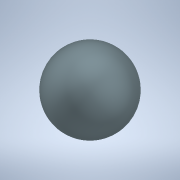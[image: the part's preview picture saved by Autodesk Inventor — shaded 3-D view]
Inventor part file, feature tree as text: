
AUTODESK INVENTOR PART (.ipt)
format: ipt  version: 2022 (Build 260153000, 153)  size: 121,856 bytes
history: native  units: in
note: dims shown in document units (in); Inventor stores cm internally (conversion verified against a paired STEP export)
features: revolve x1, sketch x1
ambient origin geometry x8: Origin, YZ Plane, XZ Plane, XY Plane, X Axis, Y Axis, Z Axis, Center Point
bodies: Solid1 (feature_tree)
feature tree (2):
  revolve  "Revolution1"  Angle=90.0deg
  sketch  "Sketch1"  dims[d5=0.0016in d6=90.0deg d7=180.0deg d8=90.0deg]
